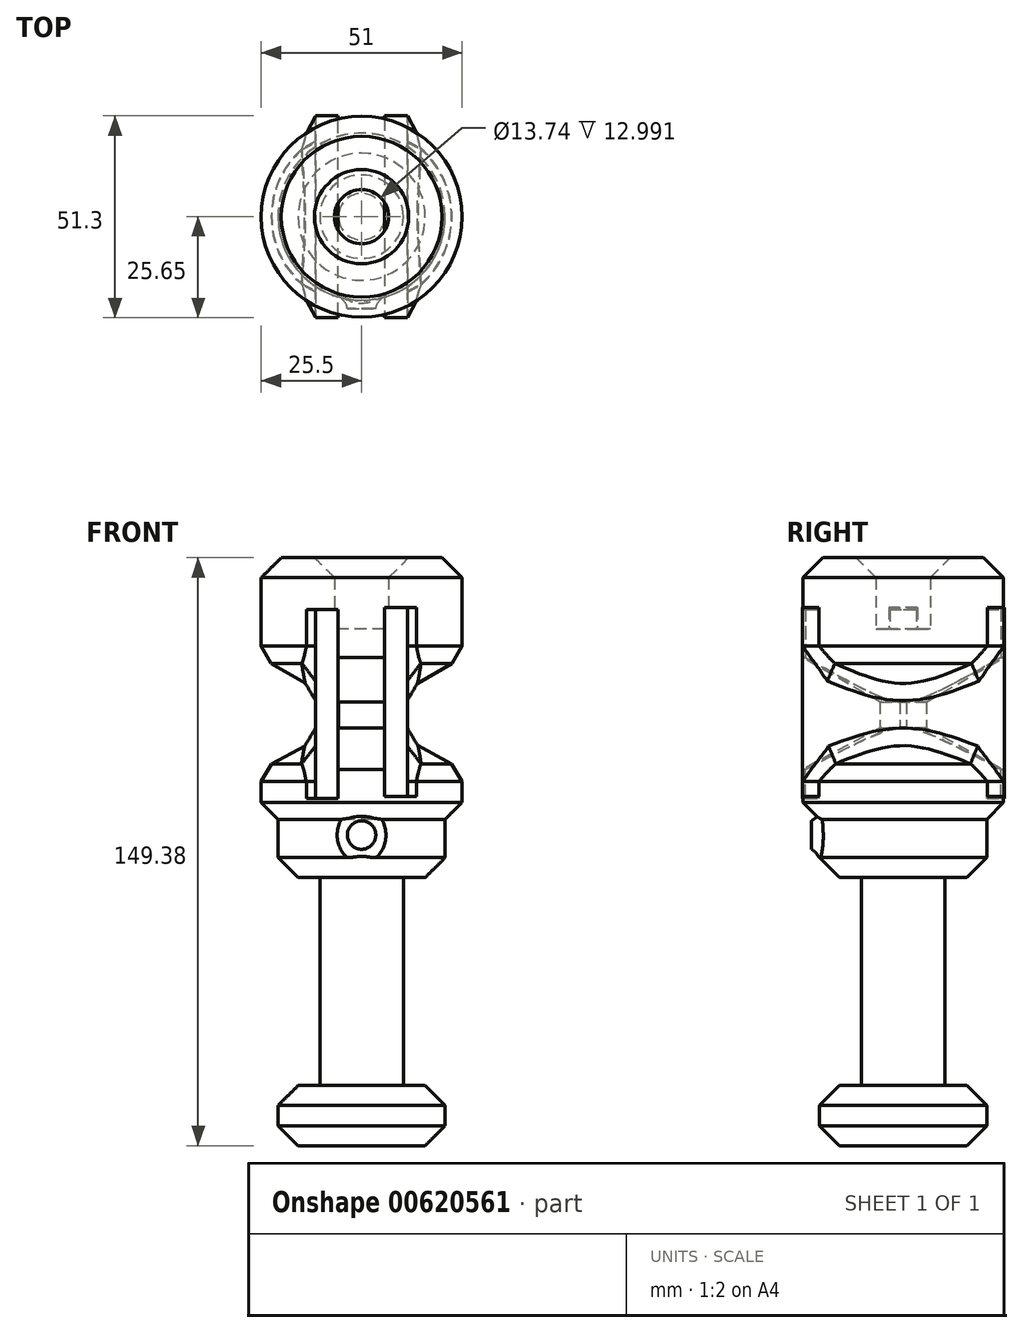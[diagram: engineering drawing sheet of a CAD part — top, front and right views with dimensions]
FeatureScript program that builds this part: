
annotation { "Feature Type Name" : "Feature", "Feature Type Description" : "" }
export const myFeature = defineFeature(function(context is Context, id is Id, definition is map)
    precondition{}
    {
        {
            var Q0;
            Q0=qCreatedBy(makeId("Front.planeOp"),FACE);
            var sketch = newSketch(context, id + "F0", { "sketchPlane" : qUnion([Q0])});
            skLineSegment(sketch, "E0", {"start": v(0, 49.01) * mm, "end": v(-25.5, 49.01) * mm});
            skLineSegment(sketch, "E1", {"start": v(0, 34.36) * mm, "end": v(-25.5, 49.01) * mm});
            skLineSegment(sketch, "E2", {"start": v(0, 49.01) * mm, "end": v(0, 34.36) * mm});
            skLineSegment(sketch, "E3", {"start": v(0, 34.36) * mm, "end": v(-25.5, 20.61) * mm});
            skLineSegment(sketch, "E4", {"start": v(-25.5, 20.61) * mm, "end": v(0, 20.61) * mm});
            skLineSegment(sketch, "E5", {"start": v(0, 20.61) * mm, "end": v(0, 34.36) * mm});
            skLineSegment(sketch, "E6", {"start": v(-6.87, 49.01) * mm, "end": v(-6.87, 56.34) * mm});
            skLineSegment(sketch, "E7", {"start": v(-6.87, 56.34) * mm, "end": v(0, 56.34) * mm});
            skLineSegment(sketch, "E8", {"start": v(0, 56.34) * mm, "end": v(0, 49.01) * mm});
            skLineSegment(sketch, "E9", {"start": v(-6.87, 20.61) * mm, "end": v(-6.87, 7.79) * mm});
            skLineSegment(sketch, "E10", {"start": v(-6.87, 7.79) * mm, "end": v(-21.22, 7.79) * mm});
            skLineSegment(sketch, "E11", {"start": v(-21.22, 7.79) * mm, "end": v(-21.22, -6.87) * mm});
            skLineSegment(sketch, "E12", {"start": v(-21.22, -6.87) * mm, "end": v(0, -6.87) * mm});
            skLineSegment(sketch, "E13", {"start": v(0, -6.87) * mm, "end": v(0, 20.61) * mm});
            skLineSegment(sketch, "E14", {"start": v(-6.87, -6.87) * mm, "end": v(-6.87, -59.7) * mm});
            skLineSegment(sketch, "E15", {"start": v(-21.22, -59.7) * mm, "end": v(-21.22, -74.97) * mm});
            skLineSegment(sketch, "E16", {"start": v(-21.22, -74.97) * mm, "end": v(0, -74.97) * mm});
            skLineSegment(sketch, "E17", {"start": v(0, -74.97) * mm, "end": v(0, -59.7) * mm});
            skLineSegment(sketch, "E18", {"start": v(0, -59.7) * mm, "end": v(-21.22, -59.7) * mm});
            skLineSegment(sketch, "E19", {"start": v(-6.87, -59.7) * mm, "end": v(0, -59.7) * mm});
            skLineSegment(sketch, "E20", {"start": v(0, -6.87) * mm, "end": v(0, -59.7) * mm});
            skLineSegment(sketch, "E21", {"start": v(-5.9, 37.74) * mm, "end": v(-5.9, 31.18) * mm});
            skLineSegment(sketch, "E22", {"start": v(-10.61, -6.87) * mm, "end": v(-10.61, -59.7) * mm});
            skLineSegment(sketch, "E23", {"start": v(-10.61, -59.7) * mm, "end": v(-6.87, -59.7) * mm});
            skLineSegment(sketch, "E24", {"start": v(-6.87, -6.87) * mm, "end": v(-10.61, -6.87) * mm});
            skSolve(sketch);
        }
        {
            var Q0;
            {var subQ2=sQuery(id+"F0.wireOp",EDGE,"E6");Q0=makeQuery(id+"F0.imprint","IMPRINT",FACE,{"disambiguationData":[TD([[makeQuery(id+"F0.imprint","IMPRINT",EDGE,{"derivedFrom":subQ2}),-1.0]])]});}
            var Q1;
            {var subQ3=sQuery(id+"F0.wireOp",EDGE,"E1");Q1=makeQuery(id+"F0.imprint","IMPRINT",FACE,{"disambiguationData":[TD([[makeQuery(id+"F0.imprint","IMPRINT",EDGE,{"derivedFrom":subQ3}),-1.0]])]});}
            var Q2;
            {var subQ0=sQuery(id+"F0.wireOp",EDGE,"E3");Q2=makeQuery(id+"F0.imprint","IMPRINT",FACE,{"disambiguationData":[TD([[makeQuery(id+"F0.imprint","IMPRINT",EDGE,{"derivedFrom":subQ0}),1.0]])]});}
            var Q3;
            {var subQ1=sQuery(id+"F0.wireOp",EDGE,"E9");Q3=makeQuery(id+"F0.imprint","IMPRINT",FACE,{"disambiguationData":[TD([[makeQuery(id+"F0.imprint","IMPRINT",EDGE,{"derivedFrom":subQ1}),1.0]])]});}
            var Q4;
            {var subQ2=sQuery(id+"F0.wireOp",EDGE,"E14");Q4=makeQuery(id+"F0.imprint","IMPRINT",FACE,{"disambiguationData":[TD([[makeQuery(id+"F0.imprint","IMPRINT",EDGE,{"derivedFrom":subQ2}),1.0]])]});}
            var Q5;
            Q5=makeQuery(id+"F0.imprint","IMPRINT",FACE,{"disambiguationData":[TD([[makeQuery(id+"F0.imprint","IMPRINT",EDGE,{"derivedFrom":sQuery(id+"F0.wireOp",EDGE,"E15")}),1.0]])]});
            var Q6;
            {var subQ3=sQuery(id+"F0.wireOp",EDGE,"E21");Q6=makeQuery(id+"F0.imprint","IMPRINT",FACE,{"disambiguationData":[TD([[makeQuery(id+"F0.imprint","IMPRINT",EDGE,{"derivedFrom":subQ3}),1.0]])]});}
            var Q7;
            Q7=makeQuery(id+"F0.imprint","IMPRINT",FACE,{"disambiguationData":[TD([[makeQuery(id+"F0.imprint","IMPRINT",EDGE,{"derivedFrom":sQuery(id+"F0.wireOp",EDGE,"E14")}),-1.0]])]});
            var Q8;
            Q8=sQuery(id+"F0.wireOp",EDGE,"E13");
            revolve(context, id + "F1", {"entities" : qUnion([Q0, Q1, Q2, Q3, Q4, Q5, Q6, Q7]), "axis" : qUnion([Q8]), "revolveType" : RevolveType.FULL});
        }
        {
            var Q0;
            Q0=makeQuery(id+"F1.opRevolve","SWEPT_FACE",FACE,{"disambiguationData":[OSD([sQuery(id+"F0.wireOp",EDGE,"E0")])]});
            extrude(context, id + "F2", {"entities" : qUnion([Q0]), "operationType" : NewBodyOperationType.ADD, "depth" : 25.4 * mm, "offsetDistance" : 25.4 * mm});
        }
        {
            var Q0;
            Q0=makeQuery(id+"F1.opRevolve","SWEPT_FACE",FACE,{"disambiguationData":[OSD([sQuery(id+"F0.wireOp",EDGE,"E4")])]});
            extrude(context, id + "F3", {"entities" : qUnion([Q0]), "operationType" : NewBodyOperationType.ADD, "depth" : 13.46 * mm, "offsetDistance" : 25.4 * mm});
        }
        {
            var Q0;
            Q0=qCreatedBy(makeId("Front.planeOp"),FACE);
            var sketch = newSketch(context, id + "F4", { "sketchPlane" : qUnion([Q0])});
            skLineSegment(sketch, "E25", {"start": v(-5.97, 13.28) * mm, "end": v(-5.97, 61.23) * mm});
            skLineSegment(sketch, "E26", {"start": v(-5.97, 61.23) * mm, "end": v(-11.76, 61.23) * mm});
            skLineSegment(sketch, "E27", {"start": v(-5.97, 13.28) * mm, "end": v(-11.76, 13.28) * mm});
            skLineSegment(sketch, "E28", {"start": v(-11.76, 13.28) * mm, "end": v(-11.76, 61.23) * mm});
            skLineSegment(sketch, "E29", {"start": v(5.83, 61.71) * mm, "end": v(5.83, 13.76) * mm});
            skLineSegment(sketch, "E30", {"start": v(5.83, 13.76) * mm, "end": v(11.62, 13.76) * mm});
            skLineSegment(sketch, "E31", {"start": v(11.62, 13.76) * mm, "end": v(11.62, 61.71) * mm});
            skLineSegment(sketch, "E32", {"start": v(11.62, 61.71) * mm, "end": v(5.83, 61.71) * mm});
            skSolve(sketch);
        }
        {
            var Q0;
            Q0 = qSketchRegion(id + "F4", true);
            extrude(context, id + "F5", {"entities" : qUnion([Q0]), "operationType" : NewBodyOperationType.ADD, "endBound" : BoundingType.SYMMETRIC, "depth" : 51.3 * mm, "offsetDistance" : 25.4 * mm});
        }
        {
            var Q0;
            Q0=makeQuery(id+"F1.opRevolve","SWEPT_FACE",FACE,{"disambiguationData":[OSD([sQuery(id+"F0.wireOp",EDGE,"E16")])]});
            var Q1;
            Q1=makeQuery(id+"F1.opRevolve","SWEPT_EDGE",EDGE,{"disambiguationData":[OSD([sQuery(id+"F0.wireOp",EDGE,"E11"),sQuery(id+"F0.wireOp",EDGE,"E12")])]});
            var Q2;
            Q2=makeQuery(id+"F3.opExtrude","CAP_EDGE",EDGE,{"disambiguationData":[OSD([sQuery(id+"F0.wireOp",EDGE,"E3"),sQuery(id+"F0.wireOp",EDGE,"E4")])],"isStart":false});
            var Q3;
            {var subQ0=sQuery(id+"F0.wireOp",EDGE,"E1");Q3=makeQuery(id+"F5.boolean.opBoolean","SPLIT",FACE,{"disambiguationData":[TD([makeQuery(id+"F5.opExtrude","SWEPT_FACE",FACE,{"disambiguationData":[OSD([sQuery(id+"F4.wireOp",EDGE,"E28")])]})])],"derivedFrom":makeQuery(id+"F1.opRevolve","SWEPT_FACE",FACE,{"disambiguationData":[OSD([subQ0])]})});}
            var Q4;
            {var subQ0=sQuery(id+"F0.wireOp",EDGE,"E1");Q4=makeQuery(id+"F5.boolean.opBoolean","SPLIT",FACE,{"disambiguationData":[TD([makeQuery(id+"F5.opExtrude","SWEPT_FACE",FACE,{"disambiguationData":[OSD([sQuery(id+"F4.wireOp",EDGE,"E31")])]})])],"derivedFrom":makeQuery(id+"F1.opRevolve","SWEPT_FACE",FACE,{"disambiguationData":[OSD([subQ0])]})});}
            var Q5;
            {var subQ0=sQuery(id+"F0.wireOp",EDGE,"E3");Q5=makeQuery(id+"F5.boolean.opBoolean","SPLIT",FACE,{"disambiguationData":[TD([makeQuery(id+"F5.opExtrude","SWEPT_FACE",FACE,{"disambiguationData":[OSD([sQuery(id+"F4.wireOp",EDGE,"E28")])]})])],"derivedFrom":makeQuery(id+"F1.opRevolve","SWEPT_FACE",FACE,{"disambiguationData":[OSD([subQ0])]})});}
            var Q6;
            {var subQ0=sQuery(id+"F0.wireOp",EDGE,"E3");Q6=makeQuery(id+"F5.boolean.opBoolean","SPLIT",FACE,{"disambiguationData":[TD([makeQuery(id+"F5.opExtrude","SWEPT_FACE",FACE,{"disambiguationData":[OSD([sQuery(id+"F4.wireOp",EDGE,"E31")])]})])],"derivedFrom":makeQuery(id+"F1.opRevolve","SWEPT_FACE",FACE,{"disambiguationData":[OSD([subQ0])]})});}
            var Q7;
            Q7=makeQuery(id+"F2.opExtrude","CAP_FACE",FACE,{"disambiguationData":[OSD([sQuery(id+"F0.wireOp",EDGE,"E0")])],"isStart":false});
            var Q8;
            Q8=makeQuery(id+"F1.opRevolve","SWEPT_EDGE",EDGE,{"disambiguationData":[OSD([sQuery(id+"F0.wireOp",EDGE,"E15"),sQuery(id+"F0.wireOp",EDGE,"E18")])]});
            chamfer(context, id + "F6", {"entities" : qUnion([Q0, Q1, Q2, Q3, Q4, Q5, Q6, Q7, Q8]), "width" : 5.08 * mm, "tangentPropagation" : true});
        }
        {
            var Q0;
            Q0=qCreatedBy(makeId("Front.planeOp"),FACE);
            var sketch = newSketch(context, id + "F7", { "sketchPlane" : qUnion([Q0])});
            skCircle(sketch, "E33", {"center": v(0, 3.95) * mm, "radius": 3.62 * mm});
            skSolve(sketch);
        }
        {
            var Q0;
            Q0 = qSketchRegion(id + "F7", true);
            extrude(context, id + "F8", {"entities" : qUnion([Q0]), "operationType" : NewBodyOperationType.ADD, "depth" : 23.37 * mm, "offsetDistance" : 25.4 * mm});
        }
        {
            var Q0;
            Q0=makeQuery(id+"F8.boolean.opBoolean","INTERSECT",EDGE,{"derivedFrom":[makeQuery(id+"F1.opRevolve","SWEPT_FACE",FACE,{"disambiguationData":[OSD([sQuery(id+"F0.wireOp",EDGE,"E11")])]}),makeQuery(id+"F8.opExtrude","SWEPT_FACE",FACE,{"disambiguationData":[OSD([sQuery(id+"F7.wireOp",EDGE,"E33")])]})]});
            fillet(context, id + "F9", {"entities" : qUnion([Q0]), "radius" : 3.68 * mm, "tangentPropagation" : true, "allowEdgeOverflow" : false});
        }
    });
